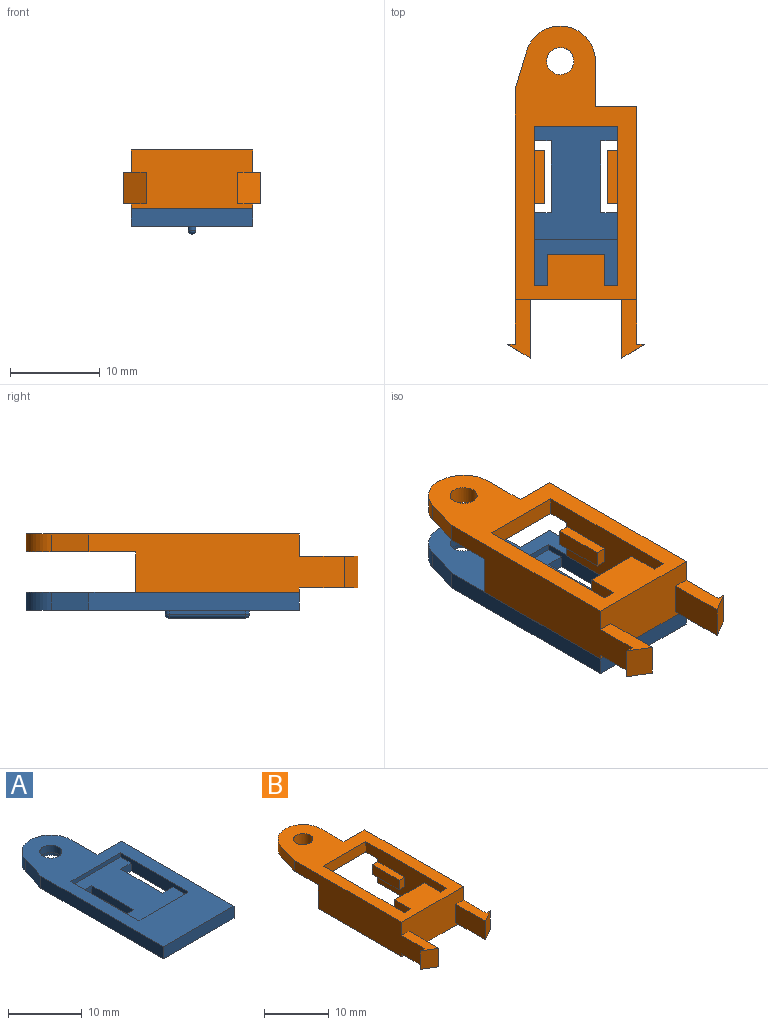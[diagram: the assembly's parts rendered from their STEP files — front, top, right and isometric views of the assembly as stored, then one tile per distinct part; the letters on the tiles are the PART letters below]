
ASSEMBLY  parts=2 mates=1
PART A: 32 faces, bbox 13.5x30.4x2.8 mm
  f0: plane 2x1.3mm, normal (0,1,0), area 2.6mm2, adj f1,f6,f7,f29
  f1: plane 8x1.3mm, normal (1,0,0), area 10.4mm2, adj f0,f5,f6,f29
  f2: plane 2x1.3mm, normal (0,-1,0), area 2.6mm2, adj f3,f6,f14,f29
  f3: plane 8x1.3mm, normal (-1,0,0), area 10.4mm2, adj f2,f4,f6,f29
  f4: plane 2x1.3mm, normal (0,1,0), area 2.6mm2, adj f3,f6,f14,f29
  f5: plane 2x1.3mm, normal (0,-1,0), area 2.6mm2, adj f1,f6,f7,f29
  f6: plane 30.4x13.5mm, normal (0,0,-1), area 305mm2, adj f0,f1,f2,f3,f4,f5,f7,f8
  f7: plane 13x2mm, normal (-1,0,0), area 19.5mm2, adj f0,f5,f6,f17,f29,f30,f31
  f8: plane 23.4x2mm, normal (-1,0,0), area 46.8mm2, adj f6,f9,f16,f17
  f9: plane 13.5x2mm, normal (0,-1,0), area 27mm2, adj f6,f8,f10,f17
  f10: plane 21.5x2mm, normal (1,0,0), area 43mm2, adj f6,f9,f11,f17
  f11: plane 4.6x2mm, normal (0,1,0), area 9.2mm2, adj f6,f10,f12,f17
  f12: plane 5x2mm, normal (1,0,0), area 10mm2, adj f6,f11,f13,f17
  f13: cylinder r=3.9mm len=7.64mm, axis (0,0,-1), area 22.2mm2, adj f6,f12,f16,f17
  f14: plane 13x2mm, normal (1,0,0), area 19.5mm2, adj f2,f4,f6,f17,f29,f30,f31
  f15: cylinder r=1.5mm len=3mm, axis (0,0,-1), area 11.3mm2, adj f17,f19
  f16: plane 4.22x2mm, normal (-0.96,0.29,0), area 8.8mm2, adj f6,f8,f13,f17
  f17: plane 30.4x13.5mm, normal (0,0,1), area 226.7mm2, adj f7,f8,f9,f10,f11,f12,f13,f14
  f18: cylinder r=2mm len=4mm, axis (0,0,-1), area 10.1mm2, adj f6,f19
  f19: plane 4x4mm, normal (0,0,-1), area 5.5mm2, adj f15,f18
  f20: plane 8.5x0.44mm, normal (-1,0,0), area 3.7mm2, adj f6,f21,f23,f25
  f21: cylinder r=0.42mm len=0.84mm, axis (0,0,1), area 0.6mm2, adj f6,f20,f22,f26
  f22: plane 8.5x0.44mm, normal (1,0,0), area 3.7mm2, adj f6,f21,f23,f28
  f23: cylinder r=0.42mm len=0.84mm, axis (0,0,1), area 0.6mm2, adj f6,f20,f22,f27
  f24: plane 8.54x0.04mm, normal (0,0,-1), area 0.3mm2, adj f25,f26,f27,f28
  f25: cylinder r=0.4mm len=8.5mm, axis (0,1,0), area 5.3mm2, adj f20,f24,f26,f27
  f26: torus R=0.02mm, axis (0,0,1), area 0.5mm2, adj f21,f24,f25,f28
  f27: torus R=0.02mm, axis (0,0,1), area 0.5mm2, adj f23,f24,f25,f28
  f28: cylinder r=0.4mm len=8.5mm, axis (0,-1,0), area 5.3mm2, adj f22,f24,f26,f27
  f29: plane 13x9.5mm, normal (0,0,1), area 91.5mm2, adj f0,f1,f2,f3,f4,f5,f7,f14
  f30: plane 9.5x0.7mm, normal (0,-1,0), area 6.7mm2, adj f7,f14,f17,f29
  f31: plane 9.5x0.7mm, normal (0,1,0), area 6.7mm2, adj f7,f14,f17,f29
PART B: 41 faces, bbox 15.2x36.9x6.5 mm
  f0: plane 3.5x0.85mm, normal (0,1,0), area 3mm2, adj f1,f7,f28,f40
  f1: plane 3.5x2.5mm, normal (-0.51,-0.86,0), area 10.2mm2, adj f0,f2,f28,f40
  f2: plane 6.5x3.5mm, normal (1,0,0), area 22.8mm2, adj f1,f10,f28,f40
  f3: plane 6.5x3.5mm, normal (-1,0,0), area 22.8mm2, adj f4,f10,f27,f39
  f4: plane 3.5x2.5mm, normal (0.51,-0.86,0), area 10.2mm2, adj f3,f5,f27,f39
  f5: plane 3.5x0.85mm, normal (0,1,0), area 3mm2, adj f4,f8,f27,f39
  f6: plane 18.2x13.5mm, normal (0,0,-1), area 109.6mm2, adj f7,f8,f10,f14,f16,f17,f18,f19
  f7: plane 28.4x6.5mm, normal (-1,0,0), area 146.2mm2, adj f0,f6,f9,f10,f23,f24,f25,f28
  f8: plane 26.5x6.5mm, normal (1,0,0), area 135.7mm2, adj f5,f6,f9,f10,f11,f24,f26,f27
  f9: plane 30.4x13.5mm, normal (0,0,1), area 208mm2, adj f7,f8,f10,f11,f12,f13,f14,f15
  f10: plane 13.5x6.5mm, normal (0,-1,0), area 76.2mm2, adj f2,f3,f6,f7,f8,f9,f27,f28
  f11: plane 4.6x2mm, normal (0,1,0), area 9.2mm2, adj f8,f9,f12,f24
  f12: plane 5x2mm, normal (1,0,0), area 10mm2, adj f9,f11,f13,f24
  f13: cylinder r=3.9mm len=7.64mm, axis (0,0,-1), area 22.2mm2, adj f9,f12,f23,f24
  f14: plane 17.7x6.5mm, normal (1,0,0), area 99.9mm2, adj f6,f9,f15,f22,f24,f25,f29,f30
  f15: plane 9.3x2mm, normal (0,-1,0), area 18.6mm2, adj f9,f14,f16,f24
  f16: plane 17.7x6.5mm, normal (-1,0,0), area 93.2mm2, adj f6,f9,f15,f17,f24,f26,f34,f35
  f17: plane 6.5x1.45mm, normal (0,1,0), area 9.4mm2, adj f6,f9,f16,f18
  f18: plane 6.5x3.5mm, normal (1,0,0), area 22.8mm2, adj f6,f9,f17,f19
  f19: plane 6.5x6.4mm, normal (0,1,0), area 41.6mm2, adj f6,f9,f18,f20
  f20: plane 6.5x3.5mm, normal (-1,0,0), area 22.8mm2, adj f6,f9,f19,f22
  f21: cylinder r=1.5mm len=3mm, axis (0,0,-1), area 18.8mm2, adj f9,f24
  f22: plane 6.5x1.45mm, normal (0,1,0), area 9.4mm2, adj f6,f9,f14,f20
  f23: plane 4.22x2mm, normal (-0.96,0.29,0), area 8.8mm2, adj f7,f9,f13,f24
  f24: plane 13.7x13.5mm, normal (0,0,-1), area 98.3mm2, adj f7,f8,f11,f12,f13,f14,f15,f16
  f25: plane 4.5x2.1mm, normal (0,1,0), area 9.5mm2, adj f6,f7,f14,f24
  f26: plane 4.5x2.1mm, normal (0,1,0), area 9.4mm2, adj f6,f8,f16,f24
  f27: plane 6.5x2.5mm, normal (0,0,1), area 10.1mm2, adj f3,f4,f5,f8,f10
  f28: plane 6.5x2.5mm, normal (0,0,1), area 10.1mm2, adj f0,f1,f2,f7,f10
  f29: plane 5.9x1.2mm, normal (0,0,1), area 7.1mm2, adj f14,f30,f32,f33
  f30: plane 1.8x1.2mm, normal (0,-1,0), area 2.2mm2, adj f14,f29,f31,f33
  f31: plane 5.9x1.2mm, normal (0,0,-1), area 7.1mm2, adj f14,f30,f32,f33
  f32: plane 1.8x1.2mm, normal (0,1,0), area 2.2mm2, adj f14,f29,f31,f33
  f33: plane 5.9x1.8mm, normal (1,0,0), area 10.6mm2, adj f29,f30,f31,f32
  f34: plane 5.9x1.2mm, normal (0,0,1), area 7.1mm2, adj f16,f35,f37,f38
  f35: plane 1.8x1.2mm, normal (0,1,0), area 2.2mm2, adj f16,f34,f36,f38
  f36: plane 5.9x1.2mm, normal (0,0,-1), area 7.1mm2, adj f16,f35,f37,f38
  f37: plane 1.8x1.2mm, normal (0,-1,0), area 2.2mm2, adj f16,f34,f36,f38
  f38: plane 5.9x1.8mm, normal (-1,0,0), area 10.6mm2, adj f34,f35,f36,f37
  f39: plane 6.5x2.5mm, normal (0,0,-1), area 10.1mm2, adj f3,f4,f5,f8,f10
  f40: plane 6.5x2.5mm, normal (0,0,-1), area 10.1mm2, adj f0,f1,f2,f7,f10
PLACE A t=(5.15,-14.86,-10.33)mm
PLACE B t=(5.15,-14.86,-8.33)mm
MATE fastened B.f6 <-> A.f17  axis (0,0,1) through (18.65,-14.86,-8.33)mm
